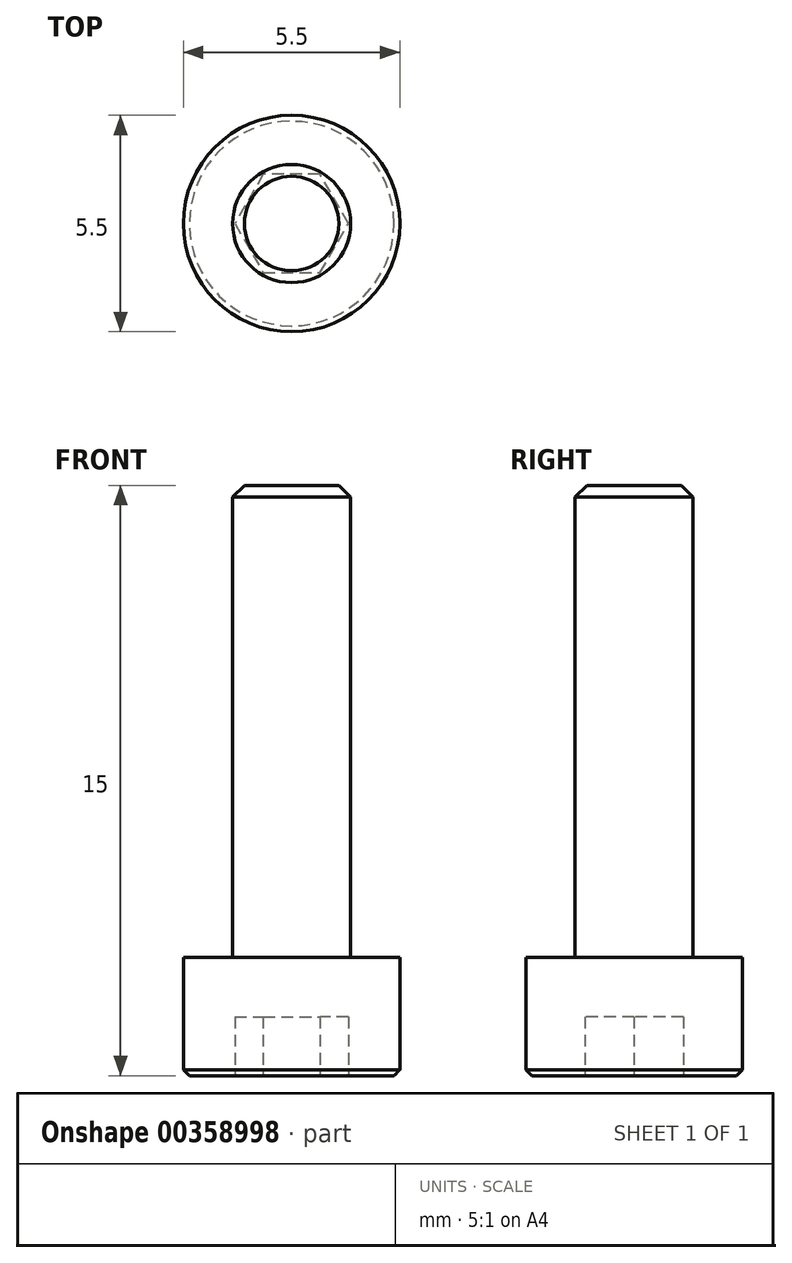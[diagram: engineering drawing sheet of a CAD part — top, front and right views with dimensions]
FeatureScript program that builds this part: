
annotation { "Feature Type Name" : "Feature", "Feature Type Description" : "" }
export const myFeature = defineFeature(function(context is Context, id is Id, definition is map)
    precondition{}
    {
        {
            assignVariable(context, id + "F0", {"name" : "d", "anyValue" : 3});
        }
        {
            assignVariable(context, id + "F1", {"name" : "a", "anyValue" : getVariable(context, 'd')});
        }
        {
            assignVariable(context, id + "F2", {"name" : "L", "anyValue" : 12});
        }
        {
            var Q0;
            Q0=qCreatedBy(makeId("Top.planeOp"),FACE);
            var sketch = newSketch(context, id + "F3", { "sketchPlane" : qUnion([Q0])});
            skCircle(sketch, "E0", {"center": v(0, 0) * mm, "radius": 2.75 * mm});
            skSolve(sketch);
        }
        {
            var Q0;
            Q0=qSketchRegion(id+"F3",true);
            extrude(context, id + "F4", {"entities" : qUnion([Q0]), "depth" : (getVariable(context, 'a')) * mm});
        }
        {
            var Q0;
            Q0=makeQuery(id+"F4.opExtrude","CAP_FACE",FACE,{"disambiguationData":[OSD([sQuery(id+"F3.wireOp",EDGE,"E0")])],"isStart":true});
            var sketch = newSketch(context, id + "F5", { "sketchPlane" : qUnion([Q0])});
            skCircle(sketch, "E1.cCircle", {"center": v(0, 0) * mm, "radius": 1.25 * mm, "construction": true});
            skLineSegment(sketch, "E1.0", {"start": v(-0.72, 1.25) * mm, "end": v(0.72, 1.25) * mm});
            skLineSegment(sketch, "E1.1", {"start": v(0.72, 1.25) * mm, "end": v(1.44, 0) * mm});
            skLineSegment(sketch, "E1.2", {"start": v(1.44, 0) * mm, "end": v(0.72, -1.25) * mm});
            skLineSegment(sketch, "E1.3", {"start": v(0.72, -1.25) * mm, "end": v(-0.72, -1.25) * mm});
            skLineSegment(sketch, "E1.4", {"start": v(-0.72, -1.25) * mm, "end": v(-1.44, 0) * mm});
            skLineSegment(sketch, "E1.5", {"start": v(-1.44, 0) * mm, "end": v(-0.72, 1.25) * mm});
            skPoint(sketch, "E1.0.midPoint", {"position": v(0, 1.25) * mm});
            skSolve(sketch);
        }
        {
            var Q0;
            Q0=qSketchRegion(id+"F5",true);
            extrude(context, id + "F6", {"entities" : qUnion([Q0]), "operationType" : NewBodyOperationType.REMOVE, "oppositeDirection" : true, "depth" : (getVariable(context, 'a') / 2) * mm});
        }
        {
            var Q0;
            Q0=makeQuery(id+"F4.opExtrude","CAP_FACE",FACE,{"disambiguationData":[OSD([sQuery(id+"F3.wireOp",EDGE,"E0")])],"isStart":false});
            var sketch = newSketch(context, id + "F7", { "sketchPlane" : qUnion([Q0])});
            skCircle(sketch, "E2", {"center": v(0, 0) * mm, "radius": 1.5 * mm});
            skSolve(sketch);
        }
        {
            var Q0;
            Q0=qSketchRegion(id+"F7",true);
            extrude(context, id + "F8", {"entities" : qUnion([Q0]), "operationType" : NewBodyOperationType.ADD, "depth" : (getVariable(context, 'L')) * mm});
        }
        {
            var Q0;
            Q0=makeQuery(id+"F4.opExtrude","CAP_EDGE",EDGE,{"disambiguationData":[OSD([sQuery(id+"F3.wireOp",EDGE,"E0")])],"isStart":true});
            var Q1;
            Q1=makeQuery(id+"F6.boolean.opBoolean","COPY",EDGE,{"derivedFrom":makeQuery(id+"F6.opExtrude","CAP_EDGE",EDGE,{"disambiguationData":[OSD([sQuery(id+"F5.wireOp",EDGE,"E1.0")])],"isStart":true})});
            var Q2;
            Q2=makeQuery(id+"F6.boolean.opBoolean","COPY",EDGE,{"derivedFrom":makeQuery(id+"F6.opExtrude","CAP_EDGE",EDGE,{"disambiguationData":[OSD([sQuery(id+"F5.wireOp",EDGE,"E1.1")])],"isStart":true})});
            var Q3;
            Q3=makeQuery(id+"F6.boolean.opBoolean","COPY",EDGE,{"derivedFrom":makeQuery(id+"F6.opExtrude","CAP_EDGE",EDGE,{"disambiguationData":[OSD([sQuery(id+"F5.wireOp",EDGE,"E1.2")])],"isStart":true})});
            var Q4;
            Q4=makeQuery(id+"F6.boolean.opBoolean","COPY",EDGE,{"derivedFrom":makeQuery(id+"F6.opExtrude","CAP_EDGE",EDGE,{"disambiguationData":[OSD([sQuery(id+"F5.wireOp",EDGE,"E1.3")])],"isStart":true})});
            var Q5;
            Q5=makeQuery(id+"F6.boolean.opBoolean","COPY",EDGE,{"derivedFrom":makeQuery(id+"F6.opExtrude","CAP_EDGE",EDGE,{"disambiguationData":[OSD([sQuery(id+"F5.wireOp",EDGE,"E1.5")])],"isStart":true})});
            var Q6;
            Q6=makeQuery(id+"F6.boolean.opBoolean","COPY",EDGE,{"derivedFrom":makeQuery(id+"F6.opExtrude","CAP_EDGE",EDGE,{"disambiguationData":[OSD([sQuery(id+"F5.wireOp",EDGE,"E1.4")])],"isStart":true})});
            chamfer(context, id + "F9", {"entities" : qUnion([Q0, Q1, Q2, Q3, Q4, Q5, Q6]), "width" : (getVariable(context, 'd') / 20) * mm, "tangentPropagation" : true});
        }
        {
            var Q0;
            Q0=makeQuery(id+"F8.opExtrude","CAP_EDGE",EDGE,{"disambiguationData":[OSD([sQuery(id+"F7.wireOp",EDGE,"E2")])],"isStart":false});
            chamfer(context, id + "F10", {"entities" : qUnion([Q0]), "width" : (getVariable(context, 'd') / 10) * mm, "tangentPropagation" : true});
        }
    });
